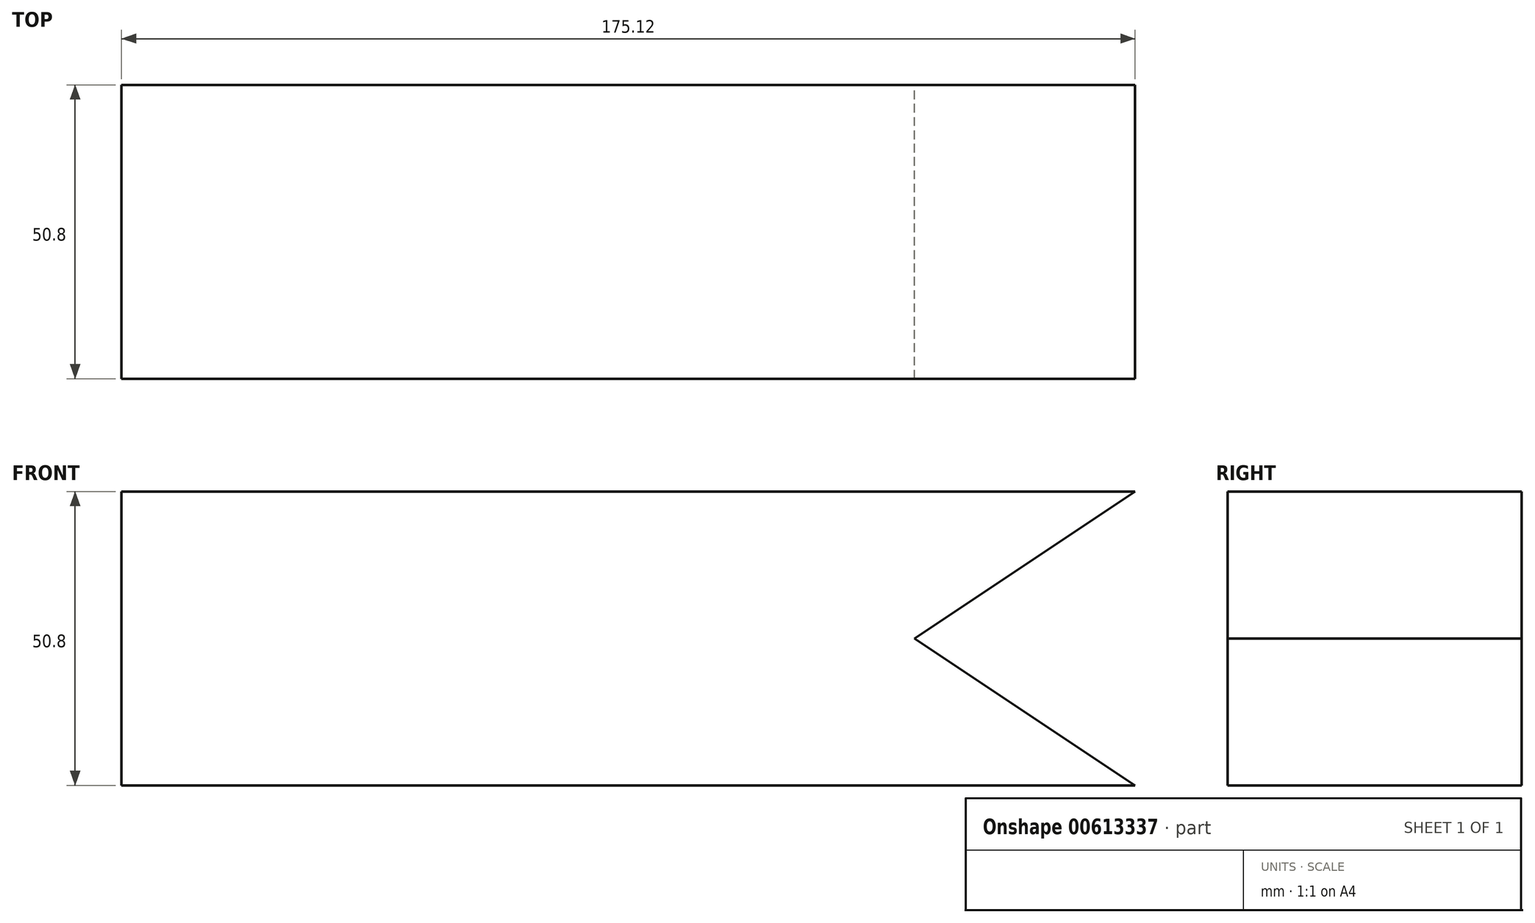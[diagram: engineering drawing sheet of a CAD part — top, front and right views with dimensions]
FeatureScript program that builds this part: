
annotation { "Feature Type Name" : "Feature", "Feature Type Description" : "" }
export const myFeature = defineFeature(function(context is Context, id is Id, definition is map)
    precondition{}
    {
        {
            var Q0;
            Q0=qCreatedBy(makeId("Front.planeOp"),FACE);
            var sketch = newSketch(context, id + "F0", { "sketchPlane" : qUnion([Q0])});
            skLineSegment(sketch, "E0.bottom", {"start": v(87.56, 25.4) * mm, "end": v(-87.56, 25.4) * mm});
            skLineSegment(sketch, "E0.top", {"start": v(87.56, -25.4) * mm, "end": v(-87.56, -25.4) * mm});
            skLineSegment(sketch, "E0.right", {"start": v(-87.56, 25.4) * mm, "end": v(-87.56, -25.4) * mm});
            skPoint(sketch, "E0.middle", {"position": v(0, 0) * mm});
            skLineSegment(sketch, "E1", {"start": v(87.56, -25.4) * mm, "end": v(49.46, 0) * mm});
            skLineSegment(sketch, "E2", {"start": v(87.56, 25.4) * mm, "end": v(49.46, 0) * mm});
            skSolve(sketch);
        }
        {
            var Q0;
            Q0 = qSketchRegion(id + "F0", true);
            extrude(context, id + "F1", {"entities" : qUnion([Q0]), "depth" : 50.8 * mm, "offsetDistance" : 25.4 * mm});
        }
    });
